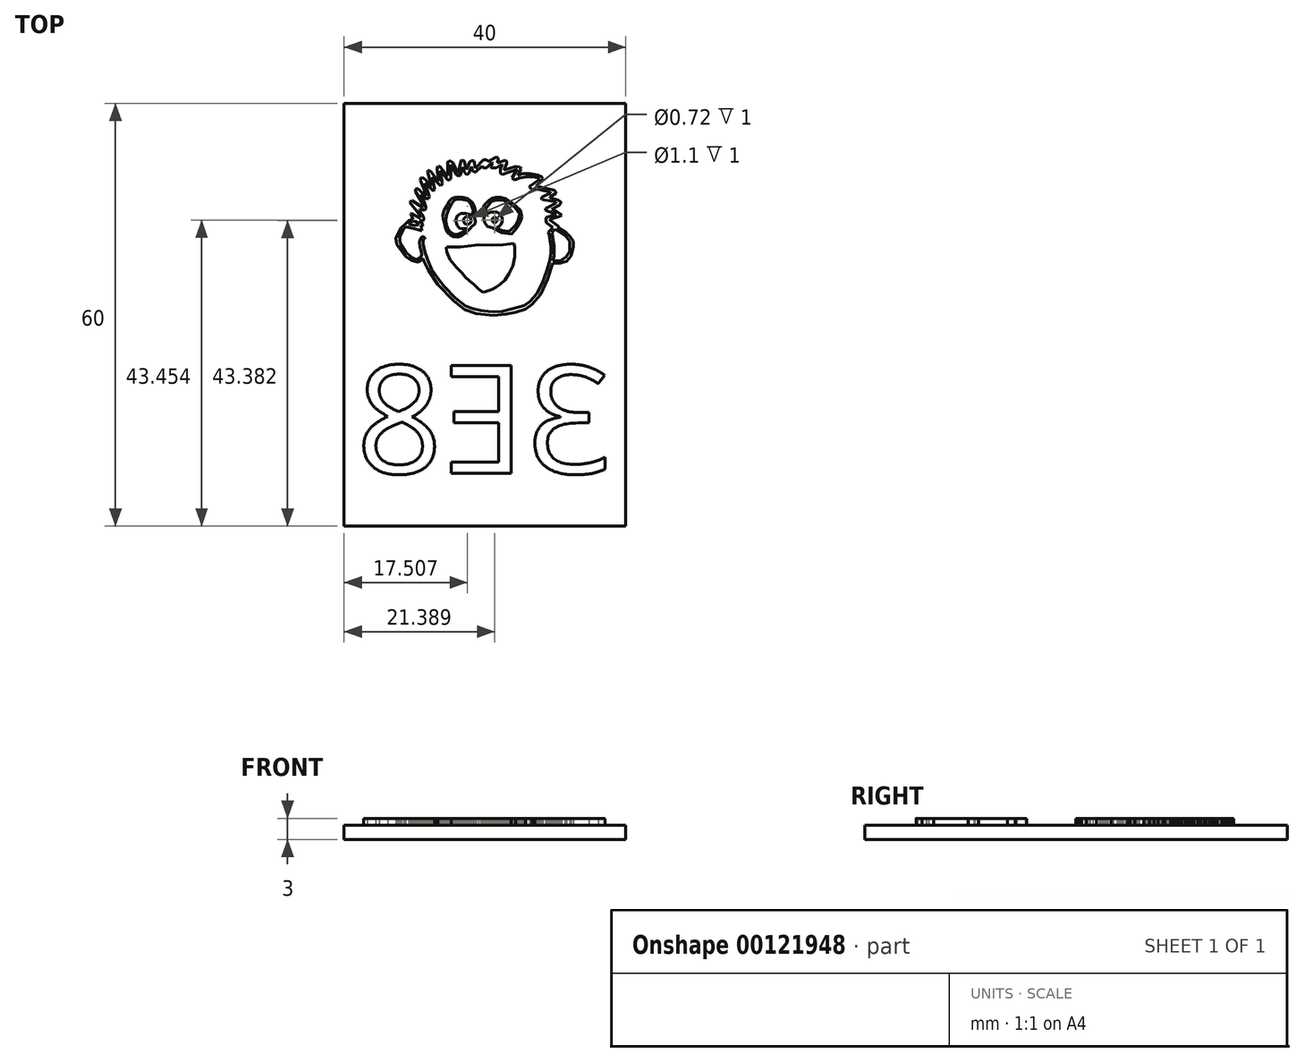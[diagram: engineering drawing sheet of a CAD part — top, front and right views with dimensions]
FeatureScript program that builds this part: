
annotation { "Feature Type Name" : "Feature", "Feature Type Description" : "" }
export const myFeature = defineFeature(function(context is Context, id is Id, definition is map)
    precondition{}
    {
        {
            var Q0;
            Q0=qCreatedBy(makeId("Top.planeOp"),FACE);
            var sketch = newSketch(context, id + "F0", { "sketchPlane" : qUnion([Q0])});
            skLineSegment(sketch, "E0.bottom", {"start": v(20, -30) * mm, "end": v(-20, -30) * mm});
            skLineSegment(sketch, "E0.top", {"start": v(20, 30) * mm, "end": v(-20, 30) * mm});
            skLineSegment(sketch, "E0.left", {"start": v(20, -30) * mm, "end": v(20, 30) * mm});
            skLineSegment(sketch, "E0.right", {"start": v(-20, -30) * mm, "end": v(-20, 30) * mm});
            skPoint(sketch, "E0.middle", {"position": v(0, 0) * mm});
            skSolve(sketch);
        }
        {
            var Q0;
            Q0 = qSketchRegion(id + "F0", true);
            extrude(context, id + "F1", {"entities" : qUnion([Q0]), "oppositeDirection" : true, "depth" : 2 * mm});
        }
        {
            var Q0;
            Q0=makeQuery(id+"F1.opExtrude","CAP_FACE",FACE,{"disambiguationData":[OSD([sQuery(id+"F0.wireOp",EDGE,"E0.bottom"),sQuery(id+"F0.wireOp",EDGE,"E0.top"),sQuery(id+"F0.wireOp",EDGE,"E0.left"),sQuery(id+"F0.wireOp",EDGE,"E0.right")])],"isStart":false});
            var sketch = newSketch(context, id + "F2", { "sketchPlane" : qUnion([Q0])});
            skLineSegment(sketch, "E1", {"start": v(-9.26, 13.42) * mm, "end": v(-10.4, 12.58) * mm});
            skLineSegment(sketch, "E2", {"start": v(-10.4, 12.58) * mm, "end": v(-10.5, 12.3) * mm});
            skLineSegment(sketch, "E3", {"start": v(-10.5, 12.3) * mm, "end": v(-11.5, 11.66) * mm});
            skLineSegment(sketch, "E4", {"start": v(-11.5, 11.66) * mm, "end": v(-12.13, 11.07) * mm});
            skLineSegment(sketch, "E5", {"start": v(-12.13, 11.07) * mm, "end": v(-12.56, 10.42) * mm});
            skLineSegment(sketch, "E6", {"start": v(-12.56, 10.42) * mm, "end": v(-12.56, 9.6) * mm});
            skLineSegment(sketch, "E7", {"start": v(-12.56, 9.6) * mm, "end": v(-12.25, 8.33) * mm});
            skLineSegment(sketch, "E8", {"start": v(-12.25, 8.33) * mm, "end": v(-11.57, 7.62) * mm});
            skLineSegment(sketch, "E9", {"start": v(-11.57, 7.62) * mm, "end": v(-10.74, 7.34) * mm});
            skLineSegment(sketch, "E10", {"start": v(-9.63, 7.34) * mm, "end": v(-8.85, 5) * mm});
            skLineSegment(sketch, "E11", {"start": v(-8.85, 5) * mm, "end": v(-7.93, 2.9) * mm});
            skLineSegment(sketch, "E12", {"start": v(-7.93, 2.9) * mm, "end": v(-6.7, 1.47) * mm});
            skLineSegment(sketch, "E13", {"start": v(-6.7, 1.47) * mm, "end": v(-5.77, 0.76) * mm});
            skLineSegment(sketch, "E14", {"start": v(-5.77, 0.76) * mm, "end": v(-4.38, 0.36) * mm});
            skLineSegment(sketch, "E15", {"start": v(-4.38, 0.36) * mm, "end": v(-3.05, 0.1) * mm});
            skLineSegment(sketch, "E16", {"start": v(-3.05, 0.1) * mm, "end": v(-1.18, -0.07) * mm});
            skLineSegment(sketch, "E17", {"start": v(-1.18, -0.07) * mm, "end": v(1.2, 0.16) * mm});
            skLineSegment(sketch, "E18", {"start": v(1.2, 0.16) * mm, "end": v(2.9, 0.73) * mm});
            skLineSegment(sketch, "E19", {"start": v(2.9, 0.73) * mm, "end": v(4.47, 1.97) * mm});
            skLineSegment(sketch, "E20", {"start": v(4.47, 1.97) * mm, "end": v(6.69, 4.31) * mm});
            skLineSegment(sketch, "E21", {"start": v(6.69, 4.31) * mm, "end": v(8, 6.32) * mm});
            skLineSegment(sketch, "E22", {"start": v(8, 6.32) * mm, "end": v(8.63, 7.6) * mm});
            skLineSegment(sketch, "E23", {"start": v(8.63, 7.6) * mm, "end": v(8.82, 8.02) * mm});
            skLineSegment(sketch, "E24", {"start": v(8.82, 8.02) * mm, "end": v(9.13, 7.64) * mm});
            skLineSegment(sketch, "E25", {"start": v(9.13, 7.64) * mm, "end": v(9.57, 7.45) * mm});
            skLineSegment(sketch, "E26", {"start": v(9.57, 7.45) * mm, "end": v(10.44, 7.69) * mm});
            skLineSegment(sketch, "E27", {"start": v(10.44, 7.69) * mm, "end": v(11.26, 8.28) * mm});
            skLineSegment(sketch, "E28", {"start": v(11.26, 8.28) * mm, "end": v(12.5, 10.03) * mm});
            skLineSegment(sketch, "E29", {"start": v(12.5, 10.03) * mm, "end": v(12.65, 10.9) * mm});
            skLineSegment(sketch, "E30", {"start": v(12.65, 10.9) * mm, "end": v(11.9, 12.37) * mm});
            skLineSegment(sketch, "E31", {"start": v(11.9, 12.37) * mm, "end": v(11.26, 12.95) * mm});
            skLineSegment(sketch, "E32", {"start": v(11.26, 12.95) * mm, "end": v(10.8, 13.37) * mm});
            skLineSegment(sketch, "E33", {"start": v(10.8, 13.37) * mm, "end": v(10.32, 13.56) * mm});
            skLineSegment(sketch, "E34", {"start": v(10.32, 13.56) * mm, "end": v(10.18, 13.56) * mm});
            skLineSegment(sketch, "E35", {"start": v(10.18, 13.56) * mm, "end": v(10.53, 14.33) * mm});
            skLineSegment(sketch, "E36", {"start": v(10.53, 14.33) * mm, "end": v(10.42, 14.38) * mm});
            skLineSegment(sketch, "E37", {"start": v(10.42, 14.38) * mm, "end": v(9.6, 13.96) * mm});
            skLineSegment(sketch, "E38", {"start": v(9.6, 13.96) * mm, "end": v(9.4, 13.77) * mm});
            skLineSegment(sketch, "E39", {"start": v(9.4, 13.77) * mm, "end": v(9.15, 13.77) * mm});
            skLineSegment(sketch, "E40", {"start": v(9.15, 13.77) * mm, "end": v(9.3, 14.2) * mm});
            skLineSegment(sketch, "E41", {"start": v(9.3, 14.2) * mm, "end": v(9.95, 14.99) * mm});
            skLineSegment(sketch, "E42", {"start": v(9.95, 14.99) * mm, "end": v(10.7, 15.99) * mm});
            skLineSegment(sketch, "E43", {"start": v(10.7, 15.99) * mm, "end": v(10.4, 16.2) * mm});
            skLineSegment(sketch, "E44", {"start": v(10.4, 16.2) * mm, "end": v(8.88, 15.27) * mm});
            skLineSegment(sketch, "E45", {"start": v(8.88, 15.27) * mm, "end": v(8.75, 15.32) * mm});
            skLineSegment(sketch, "E46", {"start": v(8.75, 15.32) * mm, "end": v(8.8, 15.64) * mm});
            skLineSegment(sketch, "E47", {"start": v(8.8, 15.64) * mm, "end": v(9.86, 17.49) * mm});
            skLineSegment(sketch, "E48", {"start": v(9.86, 17.49) * mm, "end": v(9.86, 17.79) * mm});
            skLineSegment(sketch, "E49", {"start": v(9.86, 17.79) * mm, "end": v(9.72, 17.9) * mm});
            skLineSegment(sketch, "E50", {"start": v(9.72, 17.9) * mm, "end": v(9.49, 17.85) * mm});
            skLineSegment(sketch, "E51", {"start": v(9.49, 17.85) * mm, "end": v(8.47, 16.9) * mm});
            skLineSegment(sketch, "E52", {"start": v(8.47, 16.9) * mm, "end": v(8.37, 16.9) * mm});
            skLineSegment(sketch, "E53", {"start": v(8.37, 16.9) * mm, "end": v(8.37, 17.05) * mm});
            skLineSegment(sketch, "E54", {"start": v(8.37, 17.05) * mm, "end": v(9.17, 19.07) * mm});
            skLineSegment(sketch, "E55", {"start": v(9.17, 19.07) * mm, "end": v(9.1, 19.4) * mm});
            skLineSegment(sketch, "E56", {"start": v(9.1, 19.4) * mm, "end": v(8.92, 19.54) * mm});
            skLineSegment(sketch, "E57", {"start": v(8.92, 19.54) * mm, "end": v(8.42, 19.15) * mm});
            skLineSegment(sketch, "E58", {"start": v(8.42, 19.15) * mm, "end": v(7.69, 18.29) * mm});
            skLineSegment(sketch, "E59", {"start": v(7.69, 18.29) * mm, "end": v(7.58, 18.29) * mm});
            skLineSegment(sketch, "E60", {"start": v(7.58, 18.29) * mm, "end": v(8.16, 20.29) * mm});
            skLineSegment(sketch, "E61", {"start": v(8.16, 20.29) * mm, "end": v(8.09, 20.45) * mm});
            skLineSegment(sketch, "E62", {"start": v(8.09, 20.45) * mm, "end": v(7.89, 20.45) * mm});
            skLineSegment(sketch, "E63", {"start": v(7.89, 20.45) * mm, "end": v(7.66, 20.28) * mm});
            skLineSegment(sketch, "E64", {"start": v(7.66, 20.28) * mm, "end": v(6.69, 19) * mm});
            skLineSegment(sketch, "E65", {"start": v(6.69, 19) * mm, "end": v(6.58, 19) * mm});
            skLineSegment(sketch, "E66", {"start": v(6.58, 19) * mm, "end": v(6.82, 20.73) * mm});
            skLineSegment(sketch, "E67", {"start": v(6.82, 20.73) * mm, "end": v(6.64, 21.06) * mm});
            skLineSegment(sketch, "E68", {"start": v(6.64, 21.06) * mm, "end": v(6.4, 21.06) * mm});
            skLineSegment(sketch, "E69", {"start": v(6.4, 21.06) * mm, "end": v(5.4, 19.77) * mm});
            skLineSegment(sketch, "E70", {"start": v(5.4, 19.77) * mm, "end": v(5.26, 19.77) * mm});
            skLineSegment(sketch, "E71", {"start": v(5.26, 19.77) * mm, "end": v(5.31, 20.7) * mm});
            skLineSegment(sketch, "E72", {"start": v(5.31, 20.7) * mm, "end": v(5.31, 21.67) * mm});
            skLineSegment(sketch, "E73", {"start": v(5.31, 21.67) * mm, "end": v(5.13, 21.84) * mm});
            skLineSegment(sketch, "E74", {"start": v(5.13, 21.84) * mm, "end": v(4.85, 21.84) * mm});
            skLineSegment(sketch, "E75", {"start": v(4.85, 21.84) * mm, "end": v(4.61, 21.6) * mm});
            skLineSegment(sketch, "E76", {"start": v(4.61, 21.6) * mm, "end": v(3.84, 20.16) * mm});
            skLineSegment(sketch, "E77", {"start": v(3.84, 20.16) * mm, "end": v(3.75, 20.21) * mm});
            skLineSegment(sketch, "E78", {"start": v(3.75, 20.21) * mm, "end": v(3.41, 21.9) * mm});
            skLineSegment(sketch, "E79", {"start": v(3.41, 21.9) * mm, "end": v(3.2, 22) * mm});
            skLineSegment(sketch, "E80", {"start": v(3.2, 22) * mm, "end": v(2.94, 21.8) * mm});
            skLineSegment(sketch, "E81", {"start": v(2.94, 21.8) * mm, "end": v(2.6, 20.57) * mm});
            skLineSegment(sketch, "E82", {"start": v(2.6, 20.57) * mm, "end": v(2.17, 21.7) * mm});
            skLineSegment(sketch, "E83", {"start": v(2.17, 21.7) * mm, "end": v(1.94, 21.87) * mm});
            skLineSegment(sketch, "E84", {"start": v(1.94, 21.87) * mm, "end": v(1.7, 21.87) * mm});
            skLineSegment(sketch, "E85", {"start": v(1.7, 21.87) * mm, "end": v(1.52, 21.79) * mm});
            skLineSegment(sketch, "E86", {"start": v(1.52, 21.79) * mm, "end": v(1.32, 20.82) * mm});
            skLineSegment(sketch, "E87", {"start": v(1.32, 20.82) * mm, "end": v(0.2, 22.03) * mm});
            skLineSegment(sketch, "E88", {"start": v(0.2, 22.03) * mm, "end": v(-0.27, 22.03) * mm});
            skLineSegment(sketch, "E89", {"start": v(-0.27, 22.03) * mm, "end": v(-0.41, 21.83) * mm});
            skLineSegment(sketch, "E90", {"start": v(-0.41, 21.83) * mm, "end": v(-0.41, 21.75) * mm});
            skLineSegment(sketch, "E91", {"start": v(-0.41, 21.75) * mm, "end": v(-1.6, 22.35) * mm});
            skLineSegment(sketch, "E92", {"start": v(-1.6, 22.35) * mm, "end": v(-1.9, 22.25) * mm});
            skLineSegment(sketch, "E93", {"start": v(-1.9, 22.25) * mm, "end": v(-1.9, 22.03) * mm});
            skLineSegment(sketch, "E94", {"start": v(-1.9, 22.03) * mm, "end": v(-1.75, 21.57) * mm});
            skLineSegment(sketch, "E95", {"start": v(-1.75, 21.57) * mm, "end": v(-2.88, 21.92) * mm});
            skLineSegment(sketch, "E96", {"start": v(-2.88, 21.92) * mm, "end": v(-3.07, 21.8) * mm});
            skLineSegment(sketch, "E97", {"start": v(-3.07, 21.8) * mm, "end": v(-3.07, 21.49) * mm});
            skLineSegment(sketch, "E98", {"start": v(-3.07, 21.49) * mm, "end": v(-2.72, 20.51) * mm});
            skLineSegment(sketch, "E99", {"start": v(-2.72, 20.51) * mm, "end": v(-3.52, 20.79) * mm});
            skLineSegment(sketch, "E100", {"start": v(-3.52, 20.79) * mm, "end": v(-4.38, 21.07) * mm});
            skLineSegment(sketch, "E101", {"start": v(-4.38, 21.07) * mm, "end": v(-4.94, 20.99) * mm});
            skLineSegment(sketch, "E102", {"start": v(-4.94, 20.99) * mm, "end": v(-5.11, 20.68) * mm});
            skLineSegment(sketch, "E103", {"start": v(-5.11, 20.68) * mm, "end": v(-4.68, 19.78) * mm});
            skLineSegment(sketch, "E104", {"start": v(-4.68, 19.78) * mm, "end": v(-5.3, 20.02) * mm});
            skLineSegment(sketch, "E105", {"start": v(-5.3, 20.02) * mm, "end": v(-6.42, 20.02) * mm});
            skLineSegment(sketch, "E106", {"start": v(-6.42, 20.02) * mm, "end": v(-7.46, 19.84) * mm});
            skLineSegment(sketch, "E107", {"start": v(-7.46, 19.84) * mm, "end": v(-8.03, 19.58) * mm});
            skLineSegment(sketch, "E108", {"start": v(-8.03, 19.58) * mm, "end": v(-8.25, 19.3) * mm});
            skLineSegment(sketch, "E109", {"start": v(-8.25, 19.3) * mm, "end": v(-8.08, 18.93) * mm});
            skLineSegment(sketch, "E110", {"start": v(-8.08, 18.93) * mm, "end": v(-7.43, 18.4) * mm});
            skLineSegment(sketch, "E111", {"start": v(-7.43, 18.4) * mm, "end": v(-7.3, 18.25) * mm});
            skLineSegment(sketch, "E112", {"start": v(-7.3, 18.25) * mm, "end": v(-7.89, 18.15) * mm});
            skLineSegment(sketch, "E113", {"start": v(-7.89, 18.15) * mm, "end": v(-9.85, 17.66) * mm});
            skLineSegment(sketch, "E114", {"start": v(-9.85, 17.66) * mm, "end": v(-10.06, 17.45) * mm});
            skLineSegment(sketch, "E115", {"start": v(-10.06, 17.45) * mm, "end": v(-10.06, 17.26) * mm});
            skLineSegment(sketch, "E116", {"start": v(-10.06, 17.26) * mm, "end": v(-9.27, 16.74) * mm});
            skLineSegment(sketch, "E117", {"start": v(-9.27, 16.74) * mm, "end": v(-9.27, 16.63) * mm});
            skLineSegment(sketch, "E118", {"start": v(-9.27, 16.63) * mm, "end": v(-10.37, 16.31) * mm});
            skLineSegment(sketch, "E119", {"start": v(-10.37, 16.31) * mm, "end": v(-10.75, 16.04) * mm});
            skLineSegment(sketch, "E120", {"start": v(-10.75, 16.04) * mm, "end": v(-10.75, 15.82) * mm});
            skLineSegment(sketch, "E121", {"start": v(-10.75, 15.82) * mm, "end": v(-10.5, 15.53) * mm});
            skLineSegment(sketch, "E122", {"start": v(-10.5, 15.53) * mm, "end": v(-9.54, 15.03) * mm});
            skLineSegment(sketch, "E123", {"start": v(-9.54, 15.03) * mm, "end": v(-9.5, 14.93) * mm});
            skLineSegment(sketch, "E124", {"start": v(-9.5, 14.93) * mm, "end": v(-10.13, 14.7) * mm});
            skLineSegment(sketch, "E125", {"start": v(-10.13, 14.7) * mm, "end": v(-10.79, 14.28) * mm});
            skLineSegment(sketch, "E126", {"start": v(-10.79, 14.28) * mm, "end": v(-10.87, 14.1) * mm});
            skLineSegment(sketch, "E127", {"start": v(-10.87, 14.1) * mm, "end": v(-10.5, 13.92) * mm});
            skLineSegment(sketch, "E128", {"start": v(-10.5, 13.92) * mm, "end": v(-9.7, 13.65) * mm});
            skLineSegment(sketch, "E129", {"start": v(-9.7, 13.65) * mm, "end": v(-9.3, 13.57) * mm});
            skLineSegment(sketch, "E130", {"start": v(-9.3, 13.57) * mm, "end": v(-9.19, 13.53) * mm});
            skLineSegment(sketch, "E131", {"start": v(-9.19, 13.53) * mm, "end": v(-9.26, 13.42) * mm});
            skLineSegment(sketch, "E132", {"start": v(-10.17, 12.08) * mm, "end": v(-11.34, 11.35) * mm});
            skLineSegment(sketch, "E133", {"start": v(-11.34, 11.35) * mm, "end": v(-12.02, 10.43) * mm});
            skLineSegment(sketch, "E134", {"start": v(-12.02, 10.43) * mm, "end": v(-12.02, 8.98) * mm});
            skLineSegment(sketch, "E135", {"start": v(-12.02, 8.98) * mm, "end": v(-11.56, 8.21) * mm});
            skLineSegment(sketch, "E136", {"start": v(-11.56, 8.21) * mm, "end": v(-10.7, 7.67) * mm});
            skLineSegment(sketch, "E137", {"start": v(-10.7, 7.67) * mm, "end": v(-9.66, 7.67) * mm});
            skLineSegment(sketch, "E138", {"start": v(-9.66, 7.67) * mm, "end": v(-9.82, 8.33) * mm});
            skLineSegment(sketch, "E139", {"start": v(-9.82, 8.33) * mm, "end": v(-9.82, 9.79) * mm});
            skLineSegment(sketch, "E140", {"start": v(-9.82, 9.79) * mm, "end": v(-9.65, 10.99) * mm});
            skLineSegment(sketch, "E141", {"start": v(-9.65, 10.99) * mm, "end": v(-9.48, 11.68) * mm});
            skLineSegment(sketch, "E142", {"start": v(-9.48, 11.68) * mm, "end": v(-9.72, 11.95) * mm});
            skLineSegment(sketch, "E143", {"start": v(-9.72, 11.95) * mm, "end": v(-10.17, 12.08) * mm});
            skLineSegment(sketch, "E144", {"start": v(-4.11, 10.14) * mm, "end": v(-2.6, 9.94) * mm});
            skLineSegment(sketch, "E145", {"start": v(-2.6, 9.94) * mm, "end": v(-1.03, 9.88) * mm});
            skLineSegment(sketch, "E146", {"start": v(-1.03, 9.88) * mm, "end": v(0.92, 9.92) * mm});
            skLineSegment(sketch, "E147", {"start": v(0.92, 9.92) * mm, "end": v(3.48, 9.64) * mm});
            skLineSegment(sketch, "E148", {"start": v(3.48, 9.64) * mm, "end": v(5.42, 9.59) * mm});
            skLineSegment(sketch, "E149", {"start": v(5.42, 9.59) * mm, "end": v(5.5, 9.45) * mm});
            skLineSegment(sketch, "E150", {"start": v(5.5, 9.45) * mm, "end": v(5.4, 8.93) * mm});
            skLineSegment(sketch, "E151", {"start": v(5.4, 8.93) * mm, "end": v(4.99, 7.87) * mm});
            skLineSegment(sketch, "E152", {"start": v(4.99, 7.87) * mm, "end": v(4, 6.7) * mm});
            skLineSegment(sketch, "E153", {"start": v(4, 6.7) * mm, "end": v(3.29, 5.93) * mm});
            skLineSegment(sketch, "E154", {"start": v(3.29, 5.93) * mm, "end": v(2.73, 5.3) * mm});
            skLineSegment(sketch, "E155", {"start": v(2.73, 5.3) * mm, "end": v(2.26, 4.87) * mm});
            skLineSegment(sketch, "E156", {"start": v(2.26, 4.87) * mm, "end": v(1.56, 4.26) * mm});
            skLineSegment(sketch, "E157", {"start": v(1.56, 4.26) * mm, "end": v(0.93, 3.67) * mm});
            skLineSegment(sketch, "E158", {"start": v(0.93, 3.67) * mm, "end": v(0.4, 3.27) * mm});
            skLineSegment(sketch, "E159", {"start": v(0.4, 3.27) * mm, "end": v(0.17, 3.23) * mm});
            skLineSegment(sketch, "E160", {"start": v(0.17, 3.23) * mm, "end": v(-0.26, 3.34) * mm});
            skLineSegment(sketch, "E161", {"start": v(-0.26, 3.34) * mm, "end": v(-0.78, 3.5) * mm});
            skLineSegment(sketch, "E162", {"start": v(-0.78, 3.5) * mm, "end": v(-1.14, 3.64) * mm});
            skLineSegment(sketch, "E163", {"start": v(-1.14, 3.64) * mm, "end": v(-1.6, 3.91) * mm});
            skLineSegment(sketch, "E164", {"start": v(-1.6, 3.91) * mm, "end": v(-2.2, 4.32) * mm});
            skLineSegment(sketch, "E165", {"start": v(-2.2, 4.32) * mm, "end": v(-2.83, 4.94) * mm});
            skLineSegment(sketch, "E166", {"start": v(-2.83, 4.94) * mm, "end": v(-3.42, 5.79) * mm});
            skLineSegment(sketch, "E167", {"start": v(-3.42, 5.79) * mm, "end": v(-3.96, 6.97) * mm});
            skLineSegment(sketch, "E168", {"start": v(-3.96, 6.97) * mm, "end": v(-4.25, 8.25) * mm});
            skLineSegment(sketch, "E169", {"start": v(-4.25, 8.25) * mm, "end": v(-4.25, 9.63) * mm});
            skLineSegment(sketch, "E170", {"start": v(-4.25, 9.63) * mm, "end": v(-4.11, 10.14) * mm});
            skLineSegment(sketch, "E171", {"start": v(-9.63, 12.38) * mm, "end": v(-9.2, 11.9) * mm});
            skLineSegment(sketch, "E172", {"start": v(-9.2, 11.9) * mm, "end": v(-9.03, 11.73) * mm});
            skLineSegment(sketch, "E173", {"start": v(-9.03, 11.73) * mm, "end": v(-9.12, 11.38) * mm});
            skLineSegment(sketch, "E174", {"start": v(-9.12, 11.38) * mm, "end": v(-9.26, 10.53) * mm});
            skLineSegment(sketch, "E175", {"start": v(-9.26, 10.53) * mm, "end": v(-9.36, 9.83) * mm});
            skLineSegment(sketch, "E176", {"start": v(-9.36, 9.83) * mm, "end": v(-9.36, 8.8) * mm});
            skLineSegment(sketch, "E177", {"start": v(-9.36, 8.8) * mm, "end": v(-9.17, 7.6) * mm});
            skLineSegment(sketch, "E178", {"start": v(-9.17, 7.6) * mm, "end": v(-8.73, 6.1) * mm});
            skLineSegment(sketch, "E179", {"start": v(-8.73, 6.1) * mm, "end": v(-8.16, 4.52) * mm});
            skLineSegment(sketch, "E180", {"start": v(-8.16, 4.52) * mm, "end": v(-7.33, 2.92) * mm});
            skLineSegment(sketch, "E181", {"start": v(-7.33, 2.92) * mm, "end": v(-6.4, 1.88) * mm});
            skLineSegment(sketch, "E182", {"start": v(-6.4, 1.88) * mm, "end": v(-5.59, 1.3) * mm});
            skLineSegment(sketch, "E183", {"start": v(-5.59, 1.3) * mm, "end": v(-3.92, 0.83) * mm});
            skLineSegment(sketch, "E184", {"start": v(-3.92, 0.83) * mm, "end": v(-2.44, 0.46) * mm});
            skLineSegment(sketch, "E185", {"start": v(-2.44, 0.46) * mm, "end": v(-1.33, 0.4) * mm});
            skLineSegment(sketch, "E186", {"start": v(-1.33, 0.4) * mm, "end": v(-0.5, 0.46) * mm});
            skLineSegment(sketch, "E187", {"start": v(-0.5, 0.46) * mm, "end": v(0.58, 0.58) * mm});
            skLineSegment(sketch, "E188", {"start": v(0.58, 0.58) * mm, "end": v(1.65, 0.87) * mm});
            skLineSegment(sketch, "E189", {"start": v(1.65, 0.87) * mm, "end": v(2.72, 1.23) * mm});
            skLineSegment(sketch, "E190", {"start": v(2.72, 1.23) * mm, "end": v(4.2, 2.35) * mm});
            skLineSegment(sketch, "E191", {"start": v(4.2, 2.35) * mm, "end": v(5.8, 4.04) * mm});
            skLineSegment(sketch, "E192", {"start": v(5.8, 4.04) * mm, "end": v(6.69, 5.15) * mm});
            skLineSegment(sketch, "E193", {"start": v(6.69, 5.15) * mm, "end": v(7.57, 6.44) * mm});
            skLineSegment(sketch, "E194", {"start": v(7.57, 6.44) * mm, "end": v(8.12, 7.87) * mm});
            skLineSegment(sketch, "E195", {"start": v(8.12, 7.87) * mm, "end": v(8.54, 8.9) * mm});
            skLineSegment(sketch, "E196", {"start": v(8.54, 8.9) * mm, "end": v(8.8, 10.1) * mm});
            skLineSegment(sketch, "E197", {"start": v(8.8, 10.1) * mm, "end": v(8.8, 10.74) * mm});
            skLineSegment(sketch, "E198", {"start": v(8.8, 10.74) * mm, "end": v(8.68, 10.74) * mm});
            skLineSegment(sketch, "E199", {"start": v(8.68, 10.74) * mm, "end": v(8.56, 10.76) * mm});
            skLineSegment(sketch, "E200", {"start": v(8.56, 10.76) * mm, "end": v(8.55, 10.88) * mm});
            skLineSegment(sketch, "E201", {"start": v(8.55, 10.88) * mm, "end": v(8.74, 11.06) * mm});
            skLineSegment(sketch, "E202", {"start": v(8.74, 11.06) * mm, "end": v(8.9, 11.08) * mm});
            skLineSegment(sketch, "E203", {"start": v(8.9, 11.08) * mm, "end": v(9.05, 10.96) * mm});
            skLineSegment(sketch, "E204", {"start": v(9.05, 10.96) * mm, "end": v(9.22, 10.69) * mm});
            skLineSegment(sketch, "E205", {"start": v(9.22, 10.69) * mm, "end": v(9.3, 10.23) * mm});
            skLineSegment(sketch, "E206", {"start": v(9.3, 10.23) * mm, "end": v(9.2, 9.6) * mm});
            skLineSegment(sketch, "E207", {"start": v(9.2, 9.6) * mm, "end": v(9.05, 8.97) * mm});
            skLineSegment(sketch, "E208", {"start": v(9.05, 8.97) * mm, "end": v(8.97, 8.55) * mm});
            skLineSegment(sketch, "E209", {"start": v(8.97, 8.55) * mm, "end": v(9.1, 8.17) * mm});
            skLineSegment(sketch, "E210", {"start": v(9.1, 8.17) * mm, "end": v(9.42, 7.99) * mm});
            skLineSegment(sketch, "E211", {"start": v(9.42, 7.99) * mm, "end": v(9.77, 7.86) * mm});
            skLineSegment(sketch, "E212", {"start": v(9.77, 7.86) * mm, "end": v(10.46, 8.17) * mm});
            skLineSegment(sketch, "E213", {"start": v(10.46, 8.17) * mm, "end": v(11.27, 8.93) * mm});
            skLineSegment(sketch, "E214", {"start": v(11.27, 8.93) * mm, "end": v(11.96, 10) * mm});
            skLineSegment(sketch, "E215", {"start": v(11.96, 10) * mm, "end": v(12.12, 10.5) * mm});
            skLineSegment(sketch, "E216", {"start": v(12.12, 10.5) * mm, "end": v(12.12, 11.15) * mm});
            skLineSegment(sketch, "E217", {"start": v(12.12, 11.15) * mm, "end": v(11.5, 12.23) * mm});
            skLineSegment(sketch, "E218", {"start": v(11.5, 12.23) * mm, "end": v(11.24, 12.48) * mm});
            skLineSegment(sketch, "E219", {"start": v(11.24, 12.48) * mm, "end": v(10.62, 12.32) * mm});
            skLineSegment(sketch, "E220", {"start": v(10.62, 12.32) * mm, "end": v(9.8, 12.13) * mm});
            skLineSegment(sketch, "E221", {"start": v(9.8, 12.13) * mm, "end": v(9.14, 12) * mm});
            skLineSegment(sketch, "E222", {"start": v(9.14, 12) * mm, "end": v(9, 11.99) * mm});
            skLineSegment(sketch, "E223", {"start": v(9, 11.99) * mm, "end": v(8.99, 12.2) * mm});
            skLineSegment(sketch, "E224", {"start": v(8.99, 12.2) * mm, "end": v(9.16, 12.35) * mm});
            skLineSegment(sketch, "E225", {"start": v(9.16, 12.35) * mm, "end": v(9.01, 12.52) * mm});
            skLineSegment(sketch, "E226", {"start": v(9.01, 12.52) * mm, "end": v(8.83, 12.59) * mm});
            skLineSegment(sketch, "E227", {"start": v(8.83, 12.59) * mm, "end": v(8.83, 12.77) * mm});
            skLineSegment(sketch, "E228", {"start": v(8.83, 12.77) * mm, "end": v(9, 13.1) * mm});
            skLineSegment(sketch, "E229", {"start": v(9, 13.1) * mm, "end": v(9.3, 13.36) * mm});
            skLineSegment(sketch, "E230", {"start": v(9.3, 13.36) * mm, "end": v(8.8, 13.36) * mm});
            skLineSegment(sketch, "E231", {"start": v(8.8, 13.36) * mm, "end": v(8.66, 13.53) * mm});
            skLineSegment(sketch, "E232", {"start": v(8.66, 13.53) * mm, "end": v(8.74, 13.96) * mm});
            skLineSegment(sketch, "E233", {"start": v(8.74, 13.96) * mm, "end": v(9.14, 14.57) * mm});
            skLineSegment(sketch, "E234", {"start": v(9.14, 14.57) * mm, "end": v(9.28, 14.86) * mm});
            skLineSegment(sketch, "E235", {"start": v(9.28, 14.86) * mm, "end": v(9.2, 15) * mm});
            skLineSegment(sketch, "E236", {"start": v(9.2, 15) * mm, "end": v(8.6, 14.85) * mm});
            skLineSegment(sketch, "E237", {"start": v(8.6, 14.85) * mm, "end": v(8.38, 15) * mm});
            skLineSegment(sketch, "E238", {"start": v(8.38, 15) * mm, "end": v(8.38, 15.35) * mm});
            skLineSegment(sketch, "E239", {"start": v(8.38, 15.35) * mm, "end": v(8.64, 16.09) * mm});
            skLineSegment(sketch, "E240", {"start": v(8.64, 16.09) * mm, "end": v(9.18, 17.03) * mm});
            skLineSegment(sketch, "E241", {"start": v(9.18, 17.03) * mm, "end": v(8.3, 16.5) * mm});
            skLineSegment(sketch, "E242", {"start": v(8.3, 16.5) * mm, "end": v(8.04, 16.5) * mm});
            skLineSegment(sketch, "E243", {"start": v(8.04, 16.5) * mm, "end": v(7.9, 16.78) * mm});
            skLineSegment(sketch, "E244", {"start": v(7.9, 16.78) * mm, "end": v(8.56, 18.7) * mm});
            skLineSegment(sketch, "E245", {"start": v(8.56, 18.7) * mm, "end": v(7.43, 17.65) * mm});
            skLineSegment(sketch, "E246", {"start": v(7.43, 17.65) * mm, "end": v(7.26, 17.63) * mm});
            skLineSegment(sketch, "E247", {"start": v(7.26, 17.63) * mm, "end": v(7.12, 17.84) * mm});
            skLineSegment(sketch, "E248", {"start": v(7.12, 17.84) * mm, "end": v(7.52, 19.5) * mm});
            skLineSegment(sketch, "E249", {"start": v(7.52, 19.5) * mm, "end": v(6.3, 18.33) * mm});
            skLineSegment(sketch, "E250", {"start": v(6.3, 18.33) * mm, "end": v(6.13, 18.44) * mm});
            skLineSegment(sketch, "E251", {"start": v(6.13, 18.44) * mm, "end": v(6.03, 18.7) * mm});
            skLineSegment(sketch, "E252", {"start": v(6.03, 18.7) * mm, "end": v(6.4, 20.46) * mm});
            skLineSegment(sketch, "E253", {"start": v(6.4, 20.46) * mm, "end": v(5.27, 19.14) * mm});
            skLineSegment(sketch, "E254", {"start": v(5.27, 19.14) * mm, "end": v(5.01, 19.14) * mm});
            skLineSegment(sketch, "E255", {"start": v(5.01, 19.14) * mm, "end": v(4.85, 19.35) * mm});
            skLineSegment(sketch, "E256", {"start": v(4.85, 19.35) * mm, "end": v(4.85, 21.31) * mm});
            skLineSegment(sketch, "E257", {"start": v(4.85, 21.31) * mm, "end": v(4.05, 19.88) * mm});
            skLineSegment(sketch, "E258", {"start": v(4.05, 19.88) * mm, "end": v(3.73, 19.69) * mm});
            skLineSegment(sketch, "E259", {"start": v(3.73, 19.69) * mm, "end": v(3.53, 19.77) * mm});
            skLineSegment(sketch, "E260", {"start": v(3.53, 19.77) * mm, "end": v(3.2, 20.98) * mm});
            skLineSegment(sketch, "E261", {"start": v(3.2, 20.98) * mm, "end": v(2.97, 20.26) * mm});
            skLineSegment(sketch, "E262", {"start": v(2.97, 20.26) * mm, "end": v(2.6, 19.9) * mm});
            skLineSegment(sketch, "E263", {"start": v(2.6, 19.9) * mm, "end": v(2.32, 20.02) * mm});
            skLineSegment(sketch, "E264", {"start": v(2.32, 20.02) * mm, "end": v(1.9, 21.02) * mm});
            skLineSegment(sketch, "E265", {"start": v(1.9, 21.02) * mm, "end": v(1.77, 20.5) * mm});
            skLineSegment(sketch, "E266", {"start": v(1.77, 20.5) * mm, "end": v(1.52, 20.27) * mm});
            skLineSegment(sketch, "E267", {"start": v(1.52, 20.27) * mm, "end": v(1.31, 20.27) * mm});
            skLineSegment(sketch, "E268", {"start": v(1.31, 20.27) * mm, "end": v(0.4, 21.08) * mm});
            skLineSegment(sketch, "E269", {"start": v(0.4, 21.08) * mm, "end": v(0.21, 20.88) * mm});
            skLineSegment(sketch, "E270", {"start": v(0.21, 20.88) * mm, "end": v(-0.26, 20.88) * mm});
            skLineSegment(sketch, "E271", {"start": v(-0.26, 20.88) * mm, "end": v(-1.02, 21.6) * mm});
            skLineSegment(sketch, "E272", {"start": v(-1.02, 21.6) * mm, "end": v(-1.1, 21.51) * mm});
            skLineSegment(sketch, "E273", {"start": v(-1.1, 21.51) * mm, "end": v(-0.8, 21.02) * mm});
            skLineSegment(sketch, "E274", {"start": v(-0.8, 21.02) * mm, "end": v(-0.95, 20.84) * mm});
            skLineSegment(sketch, "E275", {"start": v(-0.95, 20.84) * mm, "end": v(-1.65, 20.84) * mm});
            skLineSegment(sketch, "E276", {"start": v(-1.65, 20.84) * mm, "end": v(-2.4, 21.34) * mm});
            skLineSegment(sketch, "E277", {"start": v(-2.4, 21.34) * mm, "end": v(-2.46, 21.25) * mm});
            skLineSegment(sketch, "E278", {"start": v(-2.46, 21.25) * mm, "end": v(-2.22, 20.78) * mm});
            skLineSegment(sketch, "E279", {"start": v(-2.22, 20.78) * mm, "end": v(-2.22, 20.1) * mm});
            skLineSegment(sketch, "E280", {"start": v(-2.22, 20.1) * mm, "end": v(-2.45, 19.93) * mm});
            skLineSegment(sketch, "E281", {"start": v(-2.45, 19.93) * mm, "end": v(-4.6, 20.66) * mm});
            skLineSegment(sketch, "E282", {"start": v(-4.6, 20.66) * mm, "end": v(-3.85, 19.47) * mm});
            skLineSegment(sketch, "E283", {"start": v(-3.85, 19.47) * mm, "end": v(-4.07, 19.2) * mm});
            skLineSegment(sketch, "E284", {"start": v(-4.07, 19.2) * mm, "end": v(-4.45, 19.2) * mm});
            skLineSegment(sketch, "E285", {"start": v(-4.45, 19.2) * mm, "end": v(-4.86, 19.42) * mm});
            skLineSegment(sketch, "E286", {"start": v(-4.86, 19.42) * mm, "end": v(-5.85, 19.6) * mm});
            skLineSegment(sketch, "E287", {"start": v(-5.85, 19.6) * mm, "end": v(-7, 19.6) * mm});
            skLineSegment(sketch, "E288", {"start": v(-7, 19.6) * mm, "end": v(-7.77, 19.36) * mm});
            skLineSegment(sketch, "E289", {"start": v(-7.77, 19.36) * mm, "end": v(-7.67, 19.16) * mm});
            skLineSegment(sketch, "E290", {"start": v(-7.67, 19.16) * mm, "end": v(-6.37, 18.26) * mm});
            skLineSegment(sketch, "E291", {"start": v(-6.37, 18.26) * mm, "end": v(-6.32, 18.05) * mm});
            skLineSegment(sketch, "E292", {"start": v(-6.32, 18.05) * mm, "end": v(-6.7, 17.84) * mm});
            skLineSegment(sketch, "E293", {"start": v(-6.7, 17.84) * mm, "end": v(-7.86, 17.76) * mm});
            skLineSegment(sketch, "E294", {"start": v(-7.86, 17.76) * mm, "end": v(-9.16, 17.42) * mm});
            skLineSegment(sketch, "E295", {"start": v(-9.16, 17.42) * mm, "end": v(-9.33, 17.42) * mm});
            skLineSegment(sketch, "E296", {"start": v(-9.33, 17.42) * mm, "end": v(-9.33, 17.3) * mm});
            skLineSegment(sketch, "E297", {"start": v(-9.33, 17.3) * mm, "end": v(-8.03, 16.66) * mm});
            skLineSegment(sketch, "E298", {"start": v(-8.03, 16.66) * mm, "end": v(-8.03, 16.45) * mm});
            skLineSegment(sketch, "E299", {"start": v(-8.03, 16.45) * mm, "end": v(-8.13, 16.38) * mm});
            skLineSegment(sketch, "E300", {"start": v(-8.13, 16.38) * mm, "end": v(-10.13, 16.04) * mm});
            skLineSegment(sketch, "E301", {"start": v(-10.13, 16.04) * mm, "end": v(-10.1, 15.87) * mm});
            skLineSegment(sketch, "E302", {"start": v(-10.1, 15.87) * mm, "end": v(-8.85, 15.19) * mm});
            skLineSegment(sketch, "E303", {"start": v(-8.85, 15.19) * mm, "end": v(-8.63, 15.05) * mm});
            skLineSegment(sketch, "E304", {"start": v(-8.63, 15.05) * mm, "end": v(-8.6, 14.84) * mm});
            skLineSegment(sketch, "E305", {"start": v(-8.6, 14.84) * mm, "end": v(-10.14, 14.27) * mm});
            skLineSegment(sketch, "E306", {"start": v(-10.14, 14.27) * mm, "end": v(-8.66, 13.84) * mm});
            skLineSegment(sketch, "E307", {"start": v(-8.66, 13.84) * mm, "end": v(-8.66, 13.37) * mm});
            skLineSegment(sketch, "E308", {"start": v(-8.66, 13.37) * mm, "end": v(-8.77, 13.03) * mm});
            skLineSegment(sketch, "E309", {"start": v(-8.77, 13.03) * mm, "end": v(-9.63, 12.38) * mm});
            skLineSegment(sketch, "E310", {"start": v(-3, 16.48) * mm, "end": v(-3.95, 15.83) * mm});
            skLineSegment(sketch, "E311", {"start": v(-3.95, 15.83) * mm, "end": v(-5.02, 14.86) * mm});
            skLineSegment(sketch, "E312", {"start": v(-5.02, 14.86) * mm, "end": v(-5.23, 13.95) * mm});
            skLineSegment(sketch, "E313", {"start": v(-5.23, 13.95) * mm, "end": v(-5.1, 13.4) * mm});
            skLineSegment(sketch, "E314", {"start": v(-5.1, 13.4) * mm, "end": v(-4.68, 12.54) * mm});
            skLineSegment(sketch, "E315", {"start": v(-4.68, 12.54) * mm, "end": v(-4.25, 11.97) * mm});
            skLineSegment(sketch, "E316", {"start": v(-4.25, 11.97) * mm, "end": v(-3.77, 11.47) * mm});
            skLineSegment(sketch, "E317", {"start": v(-3.77, 11.47) * mm, "end": v(-2.4, 11.63) * mm});
            skLineSegment(sketch, "E318", {"start": v(-2.4, 11.63) * mm, "end": v(-1.03, 12.35) * mm});
            skLineSegment(sketch, "E319", {"start": v(-1.03, 12.35) * mm, "end": v(-0.38, 12.52) * mm});
            skLineSegment(sketch, "E320", {"start": v(-0.38, 12.52) * mm, "end": v(0.05, 13.04) * mm});
            skLineSegment(sketch, "E321", {"start": v(0.05, 13.04) * mm, "end": v(0.13, 13.55) * mm});
            skLineSegment(sketch, "E322", {"start": v(0.13, 13.55) * mm, "end": v(0.08, 14.05) * mm});
            skLineSegment(sketch, "E323", {"start": v(0.08, 14.05) * mm, "end": v(0.24, 15.28) * mm});
            skLineSegment(sketch, "E324", {"start": v(0.24, 15.28) * mm, "end": v(0.07, 15.58) * mm});
            skLineSegment(sketch, "E325", {"start": v(0.07, 15.58) * mm, "end": v(-0.53, 16.24) * mm});
            skLineSegment(sketch, "E326", {"start": v(-0.53, 16.24) * mm, "end": v(-1, 16.55) * mm});
            skLineSegment(sketch, "E327", {"start": v(-1, 16.55) * mm, "end": v(-1.58, 16.66) * mm});
            skLineSegment(sketch, "E328", {"start": v(-1.58, 16.66) * mm, "end": v(-2.17, 16.66) * mm});
            skLineSegment(sketch, "E329", {"start": v(-2.17, 16.66) * mm, "end": v(-3, 16.48) * mm});
            skLineSegment(sketch, "E330", {"start": v(-0.26, 14.32) * mm, "end": v(-0.9, 14.57) * mm});
            skLineSegment(sketch, "E331", {"start": v(-0.9, 14.57) * mm, "end": v(-1.73, 14.58) * mm});
            skLineSegment(sketch, "E332", {"start": v(-1.73, 14.58) * mm, "end": v(-2.2, 14.26) * mm});
            skLineSegment(sketch, "E333", {"start": v(-2.2, 14.26) * mm, "end": v(-2.43, 13.76) * mm});
            skLineSegment(sketch, "E334", {"start": v(-2.43, 13.76) * mm, "end": v(-2.43, 13.15) * mm});
            skLineSegment(sketch, "E335", {"start": v(-2.43, 13.15) * mm, "end": v(-2.22, 12.72) * mm});
            skLineSegment(sketch, "E336", {"start": v(-2.22, 12.72) * mm, "end": v(-1.93, 12.48) * mm});
            skLineSegment(sketch, "E337", {"start": v(-1.93, 12.48) * mm, "end": v(-1.77, 12.47) * mm});
            skLineSegment(sketch, "E338", {"start": v(-1.77, 12.47) * mm, "end": v(-1.71, 12.4) * mm});
            skLineSegment(sketch, "E339", {"start": v(-1.71, 12.4) * mm, "end": v(-1.75, 12.29) * mm});
            skLineSegment(sketch, "E340", {"start": v(-1.75, 12.29) * mm, "end": v(-1.98, 12.18) * mm});
            skLineSegment(sketch, "E341", {"start": v(-1.98, 12.18) * mm, "end": v(-2.39, 11.99) * mm});
            skLineSegment(sketch, "E342", {"start": v(-2.39, 11.99) * mm, "end": v(-2.83, 11.9) * mm});
            skLineSegment(sketch, "E343", {"start": v(-2.83, 11.9) * mm, "end": v(-3.2, 11.82) * mm});
            skLineSegment(sketch, "E344", {"start": v(-3.2, 11.82) * mm, "end": v(-3.5, 11.86) * mm});
            skLineSegment(sketch, "E345", {"start": v(-3.5, 11.86) * mm, "end": v(-4.41, 12.77) * mm});
            skLineSegment(sketch, "E346", {"start": v(-4.41, 12.77) * mm, "end": v(-4.77, 13.46) * mm});
            skLineSegment(sketch, "E347", {"start": v(-4.77, 13.46) * mm, "end": v(-4.9, 14.3) * mm});
            skLineSegment(sketch, "E348", {"start": v(-4.9, 14.3) * mm, "end": v(-4.3, 15.19) * mm});
            skLineSegment(sketch, "E349", {"start": v(-4.3, 15.19) * mm, "end": v(-3.28, 15.99) * mm});
            skLineSegment(sketch, "E350", {"start": v(-3.28, 15.99) * mm, "end": v(-2.61, 16.26) * mm});
            skLineSegment(sketch, "E351", {"start": v(-2.61, 16.26) * mm, "end": v(-1.66, 16.28) * mm});
            skLineSegment(sketch, "E352", {"start": v(-1.66, 16.28) * mm, "end": v(-0.95, 16.1) * mm});
            skLineSegment(sketch, "E353", {"start": v(-0.95, 16.1) * mm, "end": v(-0.5, 15.54) * mm});
            skLineSegment(sketch, "E354", {"start": v(-0.5, 15.54) * mm, "end": v(-0.1, 15.07) * mm});
            skLineSegment(sketch, "E355", {"start": v(-0.1, 15.07) * mm, "end": v(-0.12, 14.7) * mm});
            skLineSegment(sketch, "E356", {"start": v(-0.12, 14.7) * mm, "end": v(-0.26, 14.32) * mm});
            skCircle(sketch, "E357", {"center": v(-1.38, 13.45) * mm, "radius": 0.36 * mm});
            skCircle(sketch, "E358", {"center": v(2.5, 13.38) * mm, "radius": 0.55 * mm});
            skLineSegment(sketch, "E359", {"start": v(1.77, 14.15) * mm, "end": v(1.7, 14.91) * mm});
            skLineSegment(sketch, "E360", {"start": v(1.7, 14.91) * mm, "end": v(1.97, 15.7) * mm});
            skLineSegment(sketch, "E361", {"start": v(1.97, 15.7) * mm, "end": v(2.46, 16.19) * mm});
            skLineSegment(sketch, "E362", {"start": v(2.46, 16.19) * mm, "end": v(3.1, 16.38) * mm});
            skLineSegment(sketch, "E363", {"start": v(3.1, 16.38) * mm, "end": v(3.97, 16.4) * mm});
            skLineSegment(sketch, "E364", {"start": v(3.97, 16.4) * mm, "end": v(4.33, 16.3) * mm});
            skLineSegment(sketch, "E365", {"start": v(4.33, 16.3) * mm, "end": v(4.73, 15.79) * mm});
            skLineSegment(sketch, "E366", {"start": v(4.73, 15.79) * mm, "end": v(5.11, 15.06) * mm});
            skLineSegment(sketch, "E367", {"start": v(5.11, 15.06) * mm, "end": v(5.5, 14.03) * mm});
            skLineSegment(sketch, "E368", {"start": v(5.5, 14.03) * mm, "end": v(5.54, 13.37) * mm});
            skLineSegment(sketch, "E369", {"start": v(5.54, 13.37) * mm, "end": v(5.45, 12.81) * mm});
            skLineSegment(sketch, "E370", {"start": v(5.45, 12.81) * mm, "end": v(5.21, 12.08) * mm});
            skLineSegment(sketch, "E371", {"start": v(5.21, 12.08) * mm, "end": v(5.02, 11.76) * mm});
            skLineSegment(sketch, "E372", {"start": v(5.02, 11.76) * mm, "end": v(4.55, 11.44) * mm});
            skLineSegment(sketch, "E373", {"start": v(4.55, 11.44) * mm, "end": v(3.96, 11.37) * mm});
            skLineSegment(sketch, "E374", {"start": v(3.96, 11.37) * mm, "end": v(3.3, 11.63) * mm});
            skLineSegment(sketch, "E375", {"start": v(3.3, 11.63) * mm, "end": v(2.85, 11.93) * mm});
            skLineSegment(sketch, "E376", {"start": v(2.85, 11.93) * mm, "end": v(2.6, 12.2) * mm});
            skLineSegment(sketch, "E377", {"start": v(2.6, 12.2) * mm, "end": v(3.24, 12.2) * mm});
            skLineSegment(sketch, "E378", {"start": v(3.24, 12.2) * mm, "end": v(3.65, 12.3) * mm});
            skLineSegment(sketch, "E379", {"start": v(3.65, 12.3) * mm, "end": v(3.95, 12.74) * mm});
            skLineSegment(sketch, "E380", {"start": v(3.95, 12.74) * mm, "end": v(4.15, 13.35) * mm});
            skLineSegment(sketch, "E381", {"start": v(4.15, 13.35) * mm, "end": v(3.96, 14) * mm});
            skLineSegment(sketch, "E382", {"start": v(3.96, 14) * mm, "end": v(3.43, 14.35) * mm});
            skLineSegment(sketch, "E383", {"start": v(3.43, 14.35) * mm, "end": v(2.77, 14.35) * mm});
            skLineSegment(sketch, "E384", {"start": v(2.77, 14.35) * mm, "end": v(2.2, 14.27) * mm});
            skLineSegment(sketch, "E385", {"start": v(2.2, 14.27) * mm, "end": v(1.77, 14.15) * mm});
            skLineSegment(sketch, "E386", {"start": v(1.5, 13.78) * mm, "end": v(1.39, 14.21) * mm});
            skLineSegment(sketch, "E387", {"start": v(1.39, 14.21) * mm, "end": v(1.34, 14.76) * mm});
            skLineSegment(sketch, "E388", {"start": v(1.34, 14.76) * mm, "end": v(1.52, 15.46) * mm});
            skLineSegment(sketch, "E389", {"start": v(1.52, 15.46) * mm, "end": v(1.87, 16.04) * mm});
            skLineSegment(sketch, "E390", {"start": v(1.87, 16.04) * mm, "end": v(2.42, 16.49) * mm});
            skLineSegment(sketch, "E391", {"start": v(2.42, 16.49) * mm, "end": v(3.14, 16.68) * mm});
            skLineSegment(sketch, "E392", {"start": v(3.14, 16.68) * mm, "end": v(3.74, 16.72) * mm});
            skLineSegment(sketch, "E393", {"start": v(3.74, 16.72) * mm, "end": v(4.23, 16.68) * mm});
            skLineSegment(sketch, "E394", {"start": v(4.23, 16.68) * mm, "end": v(4.74, 16.45) * mm});
            skLineSegment(sketch, "E395", {"start": v(4.74, 16.45) * mm, "end": v(5.1, 16.09) * mm});
            skLineSegment(sketch, "E396", {"start": v(5.1, 16.09) * mm, "end": v(5.38, 15.55) * mm});
            skLineSegment(sketch, "E397", {"start": v(5.38, 15.55) * mm, "end": v(5.8, 14.8) * mm});
            skLineSegment(sketch, "E398", {"start": v(5.8, 14.8) * mm, "end": v(6, 14.13) * mm});
            skLineSegment(sketch, "E399", {"start": v(6, 14.13) * mm, "end": v(5.94, 13.6) * mm});
            skLineSegment(sketch, "E400", {"start": v(5.94, 13.6) * mm, "end": v(5.76, 13) * mm});
            skLineSegment(sketch, "E401", {"start": v(5.76, 13) * mm, "end": v(5.62, 12.34) * mm});
            skLineSegment(sketch, "E402", {"start": v(5.62, 12.34) * mm, "end": v(5.38, 11.73) * mm});
            skLineSegment(sketch, "E403", {"start": v(5.38, 11.73) * mm, "end": v(4.81, 11.29) * mm});
            skLineSegment(sketch, "E404", {"start": v(4.81, 11.29) * mm, "end": v(4.45, 11.1) * mm});
            skLineSegment(sketch, "E405", {"start": v(4.45, 11.1) * mm, "end": v(3.9, 11) * mm});
            skLineSegment(sketch, "E406", {"start": v(3.9, 11) * mm, "end": v(3.35, 11.22) * mm});
            skLineSegment(sketch, "E407", {"start": v(3.35, 11.22) * mm, "end": v(2.66, 11.63) * mm});
            skLineSegment(sketch, "E408", {"start": v(2.66, 11.63) * mm, "end": v(2.13, 12.22) * mm});
            skLineSegment(sketch, "E409", {"start": v(2.13, 12.22) * mm, "end": v(1.86, 12.51) * mm});
            skLineSegment(sketch, "E410", {"start": v(1.86, 12.51) * mm, "end": v(1.44, 12.84) * mm});
            skLineSegment(sketch, "E411", {"start": v(1.44, 12.84) * mm, "end": v(1.38, 13.3) * mm});
            skLineSegment(sketch, "E412", {"start": v(1.38, 13.3) * mm, "end": v(1.5, 13.78) * mm});
            skLineSegment(sketch, "E413", {"start": v(9.88, 13.24) * mm, "end": v(9.56, 13.04) * mm});
            skLineSegment(sketch, "E414", {"start": v(9.56, 13.04) * mm, "end": v(9.36, 12.86) * mm});
            skLineSegment(sketch, "E415", {"start": v(9.36, 12.86) * mm, "end": v(9.52, 12.74) * mm});
            skLineSegment(sketch, "E416", {"start": v(9.52, 12.74) * mm, "end": v(9.96, 12.68) * mm});
            skLineSegment(sketch, "E417", {"start": v(9.96, 12.68) * mm, "end": v(10.53, 12.77) * mm});
            skLineSegment(sketch, "E418", {"start": v(10.53, 12.77) * mm, "end": v(10.83, 12.83) * mm});
            skLineSegment(sketch, "E419", {"start": v(10.83, 12.83) * mm, "end": v(10.75, 13) * mm});
            skLineSegment(sketch, "E420", {"start": v(10.75, 13) * mm, "end": v(10.51, 13.18) * mm});
            skLineSegment(sketch, "E421", {"start": v(10.51, 13.18) * mm, "end": v(10.1, 13.28) * mm});
            skLineSegment(sketch, "E422", {"start": v(10.1, 13.28) * mm, "end": v(9.88, 13.24) * mm});
            skText(sketch, "E423", { "text": "3E8", "fontName": "OpenSans-Regular.ttf"});
            skLineSegment(sketch, "E424", {"start": v(-10.74, 7.34) * mm, "end": v(-9.63, 7.34) * mm});
            const initialGuessF2  = {"E423": [-0.01807, -0.02252, 1, 0, 0.01541]};
            skSetInitialGuess(sketch, initialGuessF2);
            skSolve(sketch);
        }
        {
            var Q0;
            Q0 = qSketchRegion(id + "F2", true);
            var Q1;
            Q1=makeQuery(id+"F2.imprint","IMPRINT",FACE,{"disambiguationData":[TD([[makeQuery(id+"F2.imprint","IMPRINT",EDGE,{"derivedFrom":sQuery(id+"F2.wireOp",EDGE,"E144")}),-1.0]])]});
            var Q2;
            Q2=makeQuery(id+"F2.imprint","IMPRINT",FACE,{"disambiguationData":[TD([[makeQuery(id+"F2.imprint","IMPRINT",EDGE,{"derivedFrom":sQuery(id+"F2.wireOp",EDGE,"E310")}),1.0]])]});
            var Q3;
            Q3=makeQuery(id+"F2.imprint","IMPRINT",FACE,{"disambiguationData":[TD([[makeQuery(id+"F2.imprint","IMPRINT",EDGE,{"derivedFrom":sQuery(id+"F2.wireOp",EDGE,"E358")}),-1.0]])]});
            extrude(context, id + "F3", {"entities" : qUnion([Q0, Q1, Q2, Q3]), "operationType" : NewBodyOperationType.ADD, "oppositeDirection" : true, "depth" : 3 * mm});
        }
        {
            var Q0;
            Q0=makeQuery(id+"F1.opExtrude","SWEPT_BODY",BODY,{"disambiguationData":[OSD([sQuery(id+"F0.wireOp",EDGE,"E0.bottom"),sQuery(id+"F0.wireOp",EDGE,"E0.top"),sQuery(id+"F0.wireOp",EDGE,"E0.left"),sQuery(id+"F0.wireOp",EDGE,"E0.right")])]});
            transform(context, id + "F4", {"entities" : qUnion([Q0]), "transformType" : TransformType.TRANSLATION_3D, "dx" : 0 * mm, "dy" : 0 * mm, "dz" : 2 * mm, "makeCopy" : false});
        }
        {
            var Q0;
            Q0=makeQuery(id+"F1.opExtrude","SWEPT_BODY",BODY,{"disambiguationData":[OSD([sQuery(id+"F0.wireOp",EDGE,"E0.bottom"),sQuery(id+"F0.wireOp",EDGE,"E0.top"),sQuery(id+"F0.wireOp",EDGE,"E0.left"),sQuery(id+"F0.wireOp",EDGE,"E0.right")])]});
            var Q1;
            Q1=makeQuery(id+"F3.opExtrude","SWEPT_EDGE",EDGE,{"disambiguationData":[OSD([sQuery(id+"F2.wireOp",EDGE,"E16"),sQuery(id+"F2.wireOp",EDGE,"E17")])]});
            transform(context, id + "F5", {"entities" : qUnion([Q0]), "transformType" : TransformType.ROTATION, "transformAxis" : qUnion([Q1]), "angle" : 180 * degree, "makeCopy" : false});
        }
    });
